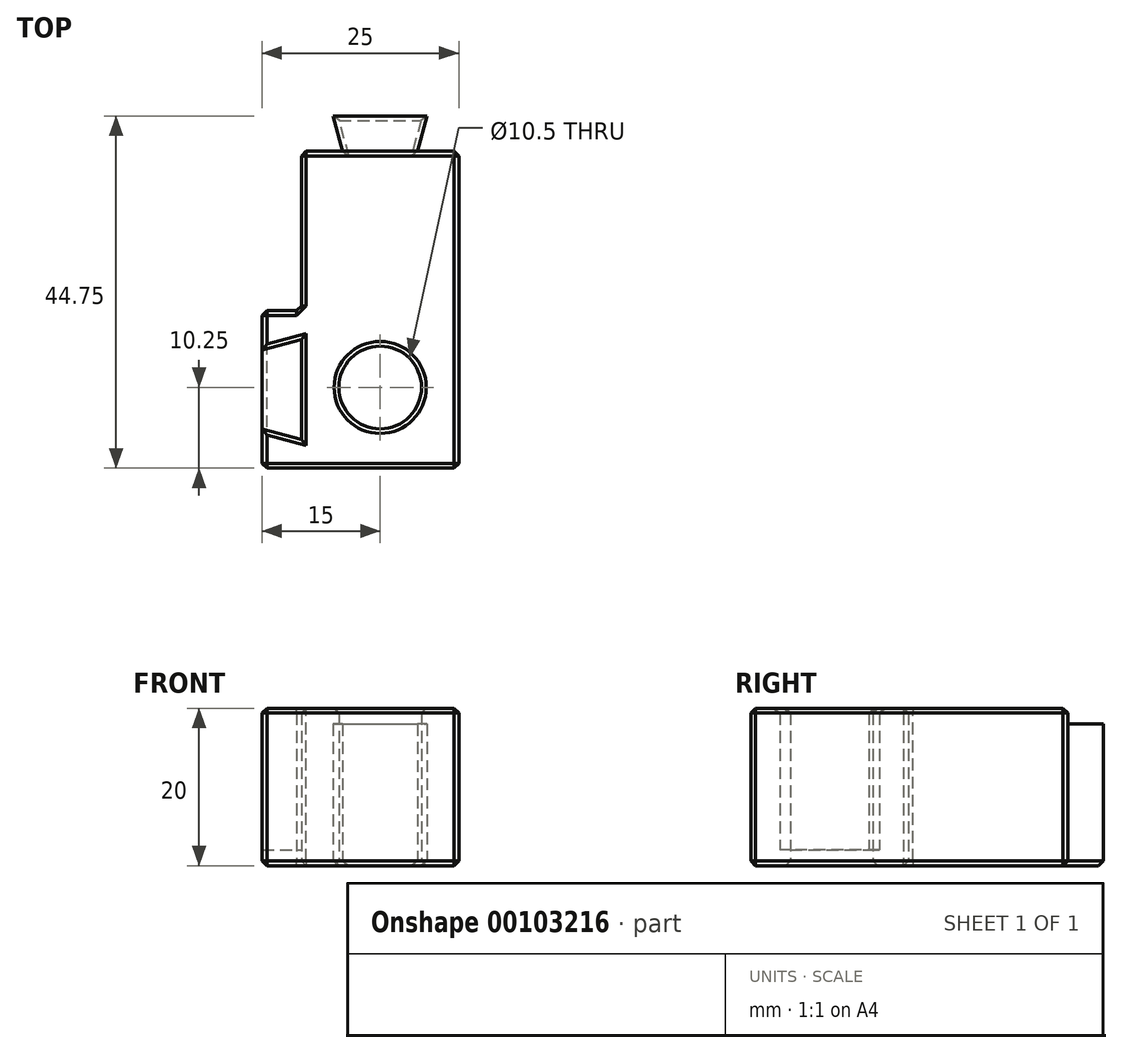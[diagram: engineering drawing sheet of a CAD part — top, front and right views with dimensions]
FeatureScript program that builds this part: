
annotation { "Feature Type Name" : "Feature", "Feature Type Description" : "" }
export const myFeature = defineFeature(function(context is Context, id is Id, definition is map)
    precondition{}
    {
        {
            assignVariable(context, id + "F0", {"name" : "ClampThickness", "anyValue" : 20});
        }
        {
            assignVariable(context, id + "F1", {"name" : "DovetailBackstopDepth", "anyValue" : 2});
        }
        {
            var Q0;
            Q0=qCreatedBy(makeId("Top.planeOp"),FACE);
            var sketch = newSketch(context, id + "F2", { "sketchPlane" : qUnion([Q0])});
            skLineSegment(sketch, "E0", {"start": v(0, 40.25) * mm, "end": v(5.25, 40.25) * mm});
            skLineSegment(sketch, "E1", {"start": v(5.25, 40.25) * mm, "end": v(4.04, 44.75) * mm});
            skLineSegment(sketch, "E2", {"start": v(4.04, 44.75) * mm, "end": v(15.96, 44.75) * mm});
            skLineSegment(sketch, "E3", {"start": v(15.96, 44.75) * mm, "end": v(14.75, 40.25) * mm});
            skLineSegment(sketch, "E4", {"start": v(14.75, 40.25) * mm, "end": v(20, 40.25) * mm});
            skLineSegment(sketch, "E5", {"start": v(0, 40.25) * mm, "end": v(0, 0) * mm});
            skLineSegment(sketch, "E6", {"start": v(0, 0) * mm, "end": v(20, 0) * mm});
            skLineSegment(sketch, "E7", {"start": v(20, 0) * mm, "end": v(20, 40.25) * mm});
            skLineSegment(sketch, "E8", {"start": v(10, 0) * mm, "end": v(10, 44.75) * mm, "construction": true});
            skCircle(sketch, "E9", {"center": v(10, 10.25) * mm, "radius": 5.25 * mm});
            skLineSegment(sketch, "E10", {"start": v(5.25, 40.25) * mm, "end": v(14.75, 40.25) * mm});
            skLineSegment(sketch, "E11", {"start": v(0, 0) * mm, "end": v(-5, 0) * mm});
            skLineSegment(sketch, "E12", {"start": v(-5, 0) * mm, "end": v(-5, 20) * mm});
            skLineSegment(sketch, "E13", {"start": v(-5, 20) * mm, "end": v(0, 20) * mm});
            skLineSegment(sketch, "E14", {"start": v(-5, 15) * mm, "end": v(0, 16.34) * mm});
            skLineSegment(sketch, "E15", {"start": v(-5, 10) * mm, "end": v(0, 10) * mm, "construction": true});
            skLineSegment(sketch, "E16.MirrorCS", {"start": v(-5, 5) * mm, "end": v(0, 3.66) * mm});
            skSolve(sketch);
        }
        {
            var Q0;
            {var subQ3=sQuery(id+"F2.wireOp",EDGE,"E0");Q0=makeQuery(id+"F2.imprint","IMPRINT",FACE,{"disambiguationData":[TD([[makeQuery(id+"F2.imprint","IMPRINT",EDGE,{"derivedFrom":subQ3}),-1.0]])]});}
            var Q1;
            {var subQ0=sQuery(id+"F2.wireOp",EDGE,"E13");Q1=makeQuery(id+"F2.imprint","IMPRINT",FACE,{"disambiguationData":[TD([[makeQuery(id+"F2.imprint","IMPRINT",EDGE,{"derivedFrom":subQ0}),-1.0]])]});}
            var Q2;
            {var subQ0=sQuery(id+"F2.wireOp",EDGE,"E11");Q2=makeQuery(id+"F2.imprint","IMPRINT",FACE,{"disambiguationData":[TD([[makeQuery(id+"F2.imprint","IMPRINT",EDGE,{"derivedFrom":subQ0}),-1.0]])]});}
            extrude(context, id + "F3", {"entities" : qUnion([Q0, Q1, Q2]), "depth" : (getVariable(context, 'ClampThickness')) * mm});
        }
        {
            var Q0;
            {var subQ0=sQuery(id+"F2.wireOp",EDGE,"E14");Q0=makeQuery(id+"F2.imprint","IMPRINT",FACE,{"disambiguationData":[TD([[makeQuery(id+"F2.imprint","IMPRINT",EDGE,{"derivedFrom":subQ0}),-1.0]])]});}
            extrude(context, id + "F4", {"entities" : qUnion([Q0]), "operationType" : NewBodyOperationType.ADD, "depth" : (getVariable(context, 'DovetailBackstopDepth')) * mm});
        }
        {
            var Q0;
            Q0=makeQuery(id+"F2.imprint","IMPRINT",FACE,{"disambiguationData":[TD([[makeQuery(id+"F2.imprint","IMPRINT",EDGE,{"derivedFrom":sQuery(id+"F2.wireOp",EDGE,"E1")}),-1.0]])]});
            extrude(context, id + "F5", {"entities" : qUnion([Q0]), "operationType" : NewBodyOperationType.ADD, "depth" : (getVariable(context, 'ClampThickness') - getVariable(context, 'DovetailBackstopDepth')) * mm});
        }
        {
            var Q0;
            {var subQ0=sQuery(id+"F2.wireOp",EDGE,"E10");var subQ1=sQuery(id+"F2.wireOp",EDGE,"E16.MirrorCS");var subQ2=sQuery(id+"F2.wireOp",EDGE,"E14");var subQ3=sQuery(id+"F2.wireOp",EDGE,"E12");var subQ4=sQuery(id+"F2.wireOp",EDGE,"E5");Q0=makeQuery(id+"F5.boolean.opBoolean","MERGE",FACE,{"derivedFrom":[makeQuery(id+"F4.boolean.opBoolean","MERGE",FACE,{"derivedFrom":[makeQuery(id+"F3.opExtrude","CAP_FACE",FACE,{"disambiguationData":[OSD([sQuery(id+"F2.wireOp",EDGE,"E0"),sQuery(id+"F2.wireOp",EDGE,"E4"),subQ4,sQuery(id+"F2.wireOp",EDGE,"E6"),sQuery(id+"F2.wireOp",EDGE,"E7"),sQuery(id+"F2.wireOp",EDGE,"E9"),subQ0,sQuery(id+"F2.wireOp",EDGE,"E11"),subQ3,sQuery(id+"F2.wireOp",EDGE,"E13"),subQ2,subQ1])],"isStart":true}),makeQuery(id+"F4.opExtrude","CAP_FACE",FACE,{"disambiguationData":[OSD([subQ4,subQ3,subQ2,subQ1])],"isStart":true})]}),makeQuery(id+"F5.opExtrude","CAP_FACE",FACE,{"disambiguationData":[OSD([sQuery(id+"F2.wireOp",EDGE,"E1"),sQuery(id+"F2.wireOp",EDGE,"E2"),sQuery(id+"F2.wireOp",EDGE,"E3"),subQ0])],"isStart":true})]});}
            var Q1;
            Q1=makeQuery(id+"F3.opExtrude","CAP_FACE",FACE,{"disambiguationData":[OSD([sQuery(id+"F2.wireOp",EDGE,"E0"),sQuery(id+"F2.wireOp",EDGE,"E4"),sQuery(id+"F2.wireOp",EDGE,"E5"),sQuery(id+"F2.wireOp",EDGE,"E6"),sQuery(id+"F2.wireOp",EDGE,"E7"),sQuery(id+"F2.wireOp",EDGE,"E9"),sQuery(id+"F2.wireOp",EDGE,"E10"),sQuery(id+"F2.wireOp",EDGE,"E11"),sQuery(id+"F2.wireOp",EDGE,"E12"),sQuery(id+"F2.wireOp",EDGE,"E13"),sQuery(id+"F2.wireOp",EDGE,"E14"),sQuery(id+"F2.wireOp",EDGE,"E16.MirrorCS")])],"isStart":false});
            var Q2;
            Q2=makeQuery(id+"F3.opExtrude","SWEPT_FACE",FACE,{"disambiguationData":[OSD([sQuery(id+"F2.wireOp",EDGE,"E6"),sQuery(id+"F2.wireOp",EDGE,"E11")])]});
            var Q3;
            Q3=makeQuery(id+"F3.opExtrude","SWEPT_FACE",FACE,{"disambiguationData":[OSD([sQuery(id+"F2.wireOp",EDGE,"E7")])]});
            var Q4;
            Q4=makeQuery(id+"F3.opExtrude","SWEPT_FACE",FACE,{"disambiguationData":[OSD([sQuery(id+"F2.wireOp",EDGE,"E13")])]});
            var Q5;
            {var subQ0=sQuery(id+"F2.wireOp",EDGE,"E5");Q5=makeQuery(id+"F3.opExtrude","SWEPT_FACE",FACE,{"disambiguationData":[OSD([subQ0]),TDD([makeQuery(id+"F2.imprint","IMPRINT",EDGE,{"disambiguationData":[TD([[makeQuery(id+"F2.imprint","INTERSECT",VERTEX,{"derivedFrom":[sQuery(id+"F2.wireOp",EDGE,"E0"),subQ0]}),-1.0]])],"derivedFrom":subQ0})])]});}
            chamfer(context, id + "F6", {"entities" : qUnion([Q0, Q1, Q2, Q3, Q4, Q5]), "width" : 0.6 * mm, "tangentPropagation" : true});
        }
    });
